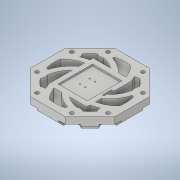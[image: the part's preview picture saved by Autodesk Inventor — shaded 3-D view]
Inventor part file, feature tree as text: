
AUTODESK INVENTOR PART (.ipt)
format: ipt  version: 2020 (Build 240168000, 168)  size: 561,664 bytes
history: native  units: in
note: dims shown in document units (in); Inventor stores cm internally (conversion verified against a paired STEP export)
features: sketch x9, extrude x7, reference x4, fillet x3, projected_geometry x3, other x3, chamfer x1, sweep x1
ambient origin geometry x8: Origin, YZ Plane, XZ Plane, XY Plane, X Axis, Y Axis, Z Axis, Center Point
bodies: Solid1 (feature_tree)
feature tree (31):
  extrude  "Extrusion1"  Depth=2.6788in
  sketch  "Sketch31"  dims[d212=0.285in d213=0.5in]
  chamfer  "Chamfer17"  Distance=1.0in
  extrude  "Extrusion26"  Depth=0.5in
  extrude  "Extrusion27"  Depth=5.0in
  extrude  "Extrusion28"  Depth=1.5748in TaperAngle=360.0deg
  extrude  "Extrusion30"  Depth=0.125in TaperAngle=0.0deg
  fillet  "Fillet5"  Radius=1.0in
  fillet  "Fillet6"  Radius=1.0in
  extrude  "Extrusion31"  Depth=0.5in TaperAngle=0.0deg
  extrude  "Extrusion32"  Depth=2.65in
  sweep  "Sweep1"
  fillet  "Fillet7"  Radius=3.5in
  sketch  "Sketch1"  dims[d0=7.0in d1=2.6788in d2=1.0in d3=0.0in]
  sketch  "Sketch32"  dims[d214=0.0in d215=5.0in]
  sketch  "Sketch33"  dims[d216=45.0deg d217=1.5748in d219=360.0deg]
  sketch  "Sketch35"  dims[d221=0.35in d222=0.125in d223=45.0deg d224=1.0in d225=0.0in d226=1.0in d227=1.0in]
  sketch  "Sketch37"  dims[d228=1.5748in d230=360.0deg d232=0.5in d233=0.0in]
  reference  "Reference1"
  reference  "Reference2"
  reference  "Reference3"
  reference  "Reference4"
  sketch  "Sketch38"  dims[d234=2.25in d235=2.65in]
  sketch  "Sketch39"  dims[d236=0.125in d237=0.0in d250=3.0in d251=3.5in]
  projected_geometry  "Projected Loop1"
  projected_geometry  "Projected Loop2"
  projected_geometry  "Projected Loop3"
  sketch  "Sketch40"  dims[d252=2.8in d253=2.8in d254=2.8in d255=2.8in d256=2.8in d257=2.8in d258=2.8in d259=2.8in d260=1.25in d261=1.25in d262=1.25in d263=1.25in d264=1.25in d265=1.25in d266=1.25in d267=1.25in d268=2.4in d269=2.4in d270=2.4in d271=2.4in d272=2.4in d273=2.4in d274=2.4in d275=2.4in d276=0.125in d277=0.0in d278=0.0625in d279=0.25in d280=5.25in d284=1.0in d289=1.5748in d291=360.0deg d293=0.09in d295=0.0in d296=0.0in d297=1.1in d298=1.25in d299=0.75in d300=0.25in d301=0.0in d302=0.7559in d303=0.25in d304=0.125in d305=0.7in d306=0.0in d307=0.0in d308=0.125in]
  other  "<userpath>\Dropbox\IREC\Drone_Full.iam"
  other  "Drone_Full.iam"
  other  "Camera:1"
